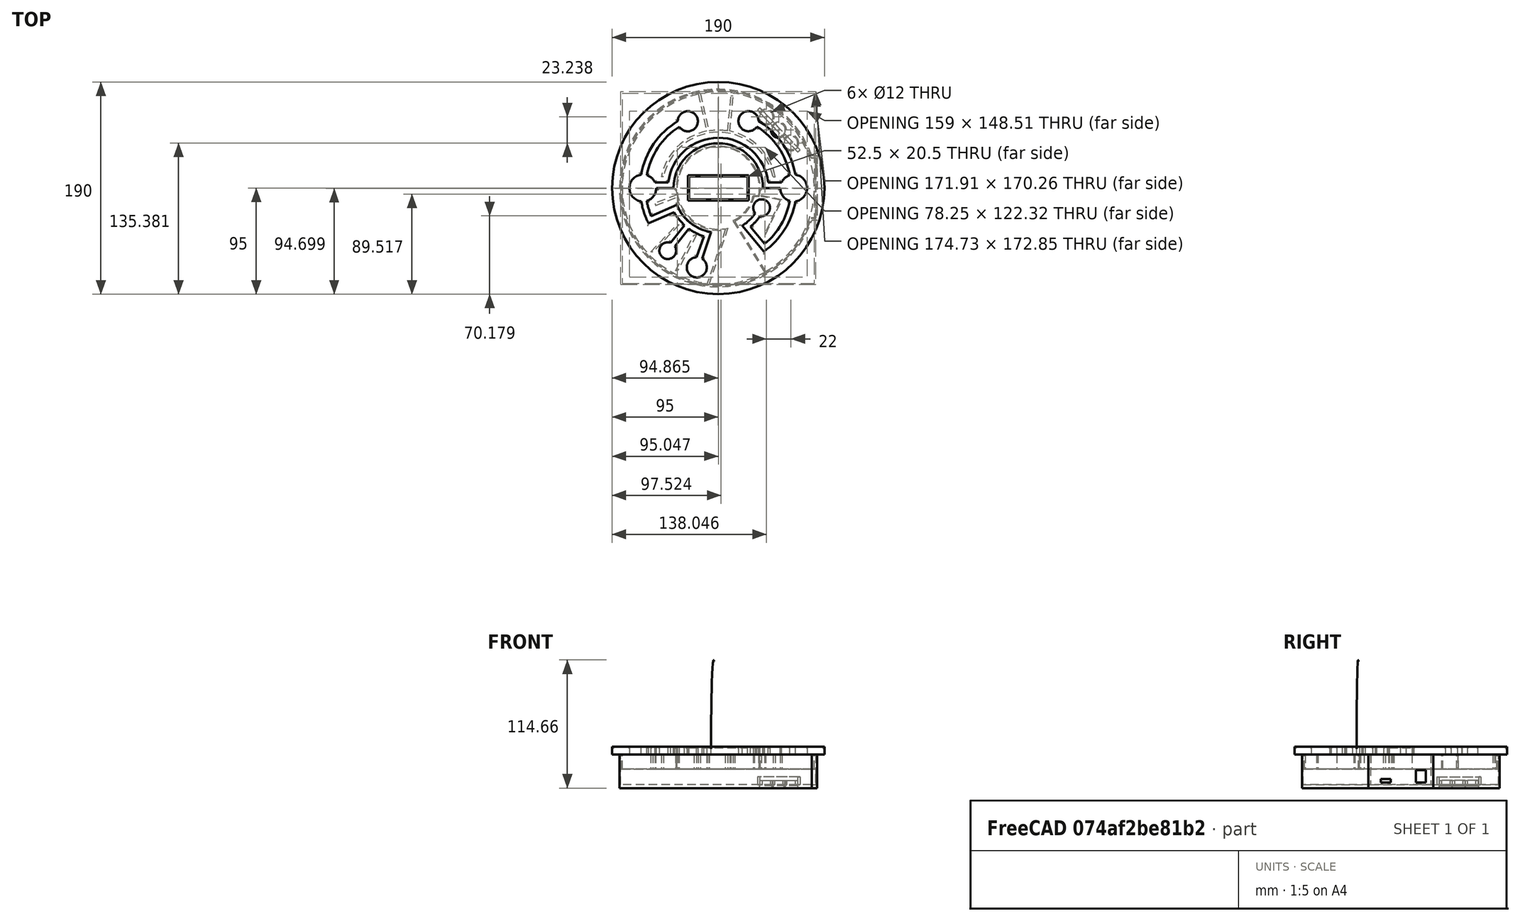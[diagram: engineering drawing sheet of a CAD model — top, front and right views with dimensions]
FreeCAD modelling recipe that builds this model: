
FCSTD DOCUMENT  (FreeCAD 0.18.4R)
Label: 3d-plate-model
License: All rights reserved
LicenseURL: http://en.wikipedia.org/wiki/All_rights_reserved
objects: Sketcher::SketchObject×11, PartDesign::Pad×7, PartDesign::Body×7, PartDesign::Pocket×4, Part::Chamfer×2, Part::Fillet×1
note: 43 computed .brp shape members not serialized (recipe doc carries the construction recipe); baked Part::Feature solids carry a one-line shape summary decoded from their .brp

FEATURE [Sketcher::SketchObject] Sketch  label="master"
  MapMode = 5
  Support = -> [XY_Plane]
  sketch-geometry (43):
    g0: Circle CenterX=9e-16 CenterY=0 CenterZ=0 NormalX=0 NormalY=0 NormalZ=1 AngleXU=0 Radius=95
    g1: LineSegment StartX=-26.25 StartY=10.25 StartZ=0 EndX=26.25 EndY=10.25 EndZ=0
    g2: LineSegment StartX=26.25 StartY=10.25 StartZ=0 EndX=26.25 EndY=-10.25 EndZ=0
    g3: LineSegment StartX=26.25 StartY=-10.25 StartZ=0 EndX=-26.25 EndY=-10.25 EndZ=0
    g4: LineSegment StartX=-26.25 StartY=-10.25 StartZ=0 EndX=-26.25 EndY=10.25 EndZ=0
    g5: ArcOfCircle CenterX=9e-16 CenterY=0 CenterZ=0 NormalX=0 NormalY=0 NormalZ=1 AngleXU=0 Radius=40 StartAngle=0 EndAngle=3.14159
    g6: LineSegment StartX=40 StartY=0 StartZ=0 EndX=55.5 EndY=1.5e-15 EndZ=0
    g7: ArcOfCircle CenterX=9e-16 CenterY=0 CenterZ=0 NormalX=0 NormalY=0 NormalZ=1 AngleXU=0 Radius=45 StartAngle=0.111341 EndAngle=3.0327
    g8: LineSegment StartX=-40 StartY=4.9e-15 StartZ=0 EndX=-55.5 EndY=-3.49e-14 EndZ=0
    g9: LineSegment StartX=-56.5417 StartY=4.89029 StartZ=0 EndX=-44.7335 EndY=4.89029 EndZ=0
    g10: LineSegment StartX=44.7214 StartY=5 StartZ=0 EndX=56.5913 EndY=5 EndZ=0
    g11: ArcOfCircle CenterX=9e-16 CenterY=0 CenterZ=0 NormalX=0 NormalY=0 NormalZ=1 AngleXU=0 Radius=65 StartAngle=0.177422 EndAngle=1.00873
    g12: ArcOfCircle CenterX=9e-16 CenterY=0 CenterZ=0 NormalX=0 NormalY=0 NormalZ=1 AngleXU=0 Radius=65 StartAngle=5.40555 EndAngle=6.10576
    g13: ArcOfCircle CenterX=27.0568 CenterY=59.8456 CenterZ=0 NormalX=0 NormalY=0 NormalZ=1 AngleXU=0 Radius=9 StartAngle=0.017152 EndAngle=5.71464
    g14: ArcOfCircle CenterX=9e-16 CenterY=0 CenterZ=0 NormalX=0 NormalY=0 NormalZ=1 AngleXU=0 Radius=70 StartAngle=5.33406 EndAngle=6.11223
    g15: LineSegment StartX=21.5122 StartY=-33.7228 StartZ=0 EndX=40.7676 EndY=-56.9035 EndZ=0
    g16: ArcOfCircle CenterX=9e-16 CenterY=0 CenterZ=0 NormalX=0 NormalY=0 NormalZ=1 AngleXU=0 Radius=40 StartAngle=5.28022 EndAngle=5.68578
    g17: ArcOfCircle CenterX=38.7698 CenterY=-17.6231 CenterZ=0 NormalX=0 NormalY=0 NormalZ=1 AngleXU=0 Radius=7.5 StartAngle=4.53097 EndAngle=10.1327
    g18: ArcOfCircle CenterX=9e-16 CenterY=0 CenterZ=0 NormalX=0 NormalY=0 NormalZ=1 AngleXU=0 Radius=45 StartAngle=5.40555 EndAngle=5.69415
    g19: LineSegment StartX=28.7537 StartY=-34.6154 StartZ=0 EndX=41.5331 EndY=-50 EndZ=0
    g20: ArcOfCircle CenterX=9e-16 CenterY=0 CenterZ=0 NormalX=0 NormalY=0 NormalZ=1 AngleXU=0 Radius=65 StartAngle=2.13603 EndAngle=2.96417
    g21: ArcOfCircle CenterX=9e-16 CenterY=0 CenterZ=0 NormalX=0 NormalY=0 NormalZ=1 AngleXU=0 Radius=65 StartAngle=3.31901 EndAngle=3.53638
    g22: ArcOfCircle CenterX=-27.2386 CenterY=59.7487 CenterZ=0 NormalX=0 NormalY=0 NormalZ=1 AngleXU=0 Radius=9 StartAngle=3.71182 EndAngle=9.40904
    g23: ArcOfCircle CenterX=9e-16 CenterY=0 CenterZ=0 NormalX=0 NormalY=0 NormalZ=1 AngleXU=0 Radius=70 StartAngle=3.31254 EndAngle=3.60903
    g24: LineSegment StartX=-37.081 StartY=-15 StartZ=0 EndX=-60 EndY=-25 EndZ=0
    g25: ArcOfCircle CenterX=9e-16 CenterY=0 CenterZ=0 NormalX=0 NormalY=0 NormalZ=1 AngleXU=0 Radius=40 StartAngle=3.52599 EndAngle=4.55135
    g26: LineSegment StartX=-62.4908 StartY=-31.542 StartZ=0 EndX=-39.5209 EndY=-21.5198 EndZ=0
    g27: ArcOfCircle CenterX=9e-16 CenterY=0 CenterZ=0 NormalX=0 NormalY=0 NormalZ=1 AngleXU=0 Radius=45 StartAngle=3.64022 EndAngle=3.97511
    g28: LineSegment StartX=-30.2523 StartY=-33.3136 StartZ=0 EndX=-42.6889 EndY=-48.9941 EndZ=0
    g29: LineSegment StartX=-38.8064 StartY=-52.1447 StartZ=0 EndX=-26.3698 EndY=-36.4641 EndZ=0
    g30: ArcOfCircle CenterX=-45.2032 CenterY=-56.0601 CenterZ=0 NormalX=0 NormalY=0 NormalZ=1 AngleXU=0 Radius=7.5 StartAngle=1.22894 EndAngle=6.83245
    g31: ArcOfCircle CenterX=9e-16 CenterY=0 CenterZ=0 NormalX=0 NormalY=0 NormalZ=1 AngleXU=0 Radius=45 StartAngle=4.08628 EndAngle=4.42118
    g32: LineSegment StartX=-12.9201 StartY=-43.1053 StartZ=0 EndX=-19.3775 EndY=-62.0487 EndZ=0
    g33: LineSegment StartX=-6.4138 StartY=-39.4824 StartZ=0 EndX=-14.55 EndY=-63.3506 EndZ=0
    g34: ArcOfCircle CenterX=-19.215 CenterY=-71.0472 CenterZ=0 NormalX=0 NormalY=0 NormalZ=1 AngleXU=0 Radius=9 StartAngle=1.58885 EndAngle=7.30908
    g35: ArcOfCircle CenterX=-67.5 CenterY=0 CenterZ=0 NormalX=0 NormalY=0 NormalZ=1 AngleXU=0 Radius=12 StartAngle=1.69441 EndAngle=4.58877
    g36: ArcOfCircle CenterX=9e-16 CenterY=0 CenterZ=0 NormalX=0 NormalY=0 NormalZ=1 AngleXU=0 Radius=70 StartAngle=2.11493 EndAngle=2.97064
    g37: ArcOfCircle CenterX=-67.5 CenterY=0 CenterZ=0 NormalX=0 NormalY=0 NormalZ=1 AngleXU=0 Radius=12 StartAngle=0.419741 EndAngle=1.27305
    g38: ArcOfCircle CenterX=-67.5 CenterY=0 CenterZ=0 NormalX=0 NormalY=0 NormalZ=1 AngleXU=0 Radius=12 StartAngle=5.01013 EndAngle=6.28319
    g39: ArcOfCircle CenterX=67.5 CenterY=0 CenterZ=0 NormalX=0 NormalY=0 NormalZ=1 AngleXU=0 Radius=12 StartAngle=4.83601 EndAngle=7.73036
    g40: ArcOfCircle CenterX=9e-16 CenterY=0 CenterZ=0 NormalX=0 NormalY=0 NormalZ=1 AngleXU=0 Radius=70 StartAngle=0.170952 EndAngle=1.0297
    g41: ArcOfCircle CenterX=67.5 CenterY=0 CenterZ=0 NormalX=0 NormalY=0 NormalZ=1 AngleXU=0 Radius=12 StartAngle=1.86854 EndAngle=2.71182
    g42: ArcOfCircle CenterX=67.5 CenterY=0 CenterZ=0 NormalX=0 NormalY=0 NormalZ=1 AngleXU=0 Radius=12 StartAngle=3.14159 EndAngle=4.41465
  constraints (133):
    c: Radius(g0) = 95
    c: Coincident(g1,g2)
    c: Coincident(g2,g3)
    c: Coincident(g3,g4)
    c: Coincident(g4,g1)
    c: Horizontal(g1)
    c: Vertical(g4)
    c: DistanceX(g1,g1) = 52.5
    c: DistanceY(g2,g2) = 20.5
    c: Symmetric(g2,g3,g-2)
    c: Symmetric(g2,g1,g-1)
    c: Radius(g5) = 40
    c: Coincident(g5,g0)
    c: Symmetric(g5,g5,g-2)
    c: Parallel(g6,g-1)
    c: PointOnObject(g5,g-1)
    c: Radius(g7) = 45
    c: Coincident(g7,g0)
    c: Parallel(g9,g8)
    c: Coincident(g7,g9)
    c: Coincident(g8,g5)
    c: Parallel(g8,g3)
    c: Coincident(g5,g6)
    c: Coincident(g10,g7)
    c: Parallel(g10,g3)
    c: DistanceY(g6,g10) = 5
    c: Coincident(g11,g0)
    c: Radius(g11) = 65
    c: Coincident(g0,g-1)
    c: Coincident(g12,g0)
    c: Radius(g12) = 65
    c: Coincident(g13,g11)
    c: Radius(g13) = 9
    c: Coincident(g14,g0)
    c: Coincident(g15,g14)
    c: Coincident(g16,g0)
    c: Coincident(g16,g15)
    c: Coincident(g17,g16)
    c: Coincident(g18,g0)
    c: Coincident(g18,g17)
    c: Radius(g16) = 40
    c: Radius(g18) = 45
    c: Coincident(g19,g12)
    c: Coincident(g19,g18)
    c: Parallel(g19,g15)
    c: Radius(g17) = 7.5
    c: Radius(g14) = 70
    c: Distance(g18,g15) = 5
    c: DistanceY(g12,g6) = 50
    c: Perpendicular(g12,g19)
    c: DistanceY(g10,g11) = 50
    c: DistanceY(g7,g13) = 55
    c: DistanceY(g17,g5) = 25
    c: DistanceY(g16,g5) = 22.5
    c: Coincident(g20,g0)
    c: Radius(g20) = 65
    c: Coincident(g21,g0)
    c: Radius(g21) = 65
    c: Coincident(g22,g20)
    c: Radius(g22) = 9
    c: Coincident(g23,g0)
    c: Radius(g23) = 70
    c: DistanceY(g7,g20) = 50
    c: DistanceY(g7,g22) = 55
    c: DistanceY(g21,g5) = 25
    c: Coincident(g24,g21)
    c: Coincident(g25,g0)
    c: Coincident(g25,g24)
    c: Radius(g25) = 40
    c: Coincident(g26,g23)
    c: Coincident(g27,g0)
    c: Radius(g27) = 45
    c: Coincident(g26,g27)
    c: Parallel(g24,g26)
    c: Distance(g26,g24) = 5
    c: DistanceY(g24,g5) = 15
    c: Coincident(g28,g27)
    c: Coincident(g28,g30)
    c: Coincident(g29,g30)
    c: Parallel(g28,g29)
    c: Distance(g29,g27) = 5
    c: Radius(g30) = 7.5
    c: Equal(g28,g29)
    c: Coincident(g31,g0)
    c: Coincident(g31,g29)
    c: Coincident(g32,g31)
    c: Coincident(g33,g25)
    c: Radius(g31) = 45
    c: Coincident(g34,g32)
    c: Parallel(g32,g33)
    c: Coincident(g34,g33)
    c: Equal(g29,g32)
    c: Radius(g34) = 9
    c: Distance(g29,g0) = 65
    c: Distance(g27,g26) = 15
    c: Distance(g23,g30) = 30
    c: Distance(g29,g31) = 15
    c: Distance(g34,g30) = 30
    c: Distance(g33,g32) = 5
    c: Distance(g33,g0) = 65
    c: Coincident(g35,g23)
    c: Distance(g35,g0) = 67.5
    c: Coincident(g36,g0)
    c: Radius(g36) = 70
    c: Coincident(g36,g22)
    c: Coincident(g36,g35)
    c: Radius(g35) = 12
    c: Coincident(g37,g35)
    c: Radius(g37) = 12
    c: Coincident(g37,g20)
    c: Coincident(g37,g9)
    c: Radius(g38) = 12
    c: Coincident(g38,g8)
    c: Coincident(g38,g21)
    c: Coincident(g38,g35)
    c: Distance(g9,g8) = 5
    c: PointOnObject(g35,g-1)
    c: Coincident(g39,g14)
    c: Distance(g39,g0) = 67.5
    c: Coincident(g40,g39)
    c: Coincident(g40,g13)
    c: Coincident(g40,g0)
    c: Radius(g40) = 70
    c: Radius(g39) = 12
    c: PointOnObject(g39,g-1)
    c: Coincident(g41,g39)
    c: Radius(g41) = 12
    c: Coincident(g11,g41)
    c: Coincident(g41,g10)
    c: Coincident(g42,g6)
    c: Coincident(g42,g12)
    c: Coincident(g42,g39)
    c: Radius(g42) = 12
FEATURE [PartDesign::Pad] Pad
  Length = 7
  Length2 = 100
  Profile = -> Sketch
  Type = 0
FEATURE [PartDesign::Body] Body
  Group = -> [Sketch,Pad]
  Origin = -> Origin
  Tip = -> Pad
FEATURE [Sketcher::SketchObject] Sketch003
  sketch-geometry (32):
    g0: ArcOfCircle CenterX=0 CenterY=0 CenterZ=0 NormalX=0 NormalY=0 NormalZ=1 AngleXU=0 Radius=50 StartAngle=0.201358 EndAngle=2.94023
    g1: LineSegment StartX=-48.9898 StartY=10 StartZ=0 EndX=-50.9898 EndY=10 EndZ=0
    g2: LineSegment StartX=48.9898 StartY=10 StartZ=0 EndX=50.9898 EndY=10 EndZ=0
    g3: ArcOfCircle CenterX=0 CenterY=0 CenterZ=0 NormalX=0 NormalY=0 NormalZ=1 AngleXU=0 Radius=51.9611 StartAngle=1.77252 EndAngle=2.94793
    g4: LineSegment StartX=-17.768 StartY=84.1445 StartZ=0 EndX=-10.4109 EndY=50.9075 EndZ=0
    g5: LineSegment StartX=-15.9186 StartY=84.5139 StartZ=0 EndX=-8.51361 EndY=51.0603 EndZ=0
    g6: ArcOfCircle CenterX=0 CenterY=0 CenterZ=0 NormalX=0 NormalY=0 NormalZ=1 AngleXU=0 Radius=51.7652 StartAngle=1.40611 EndAngle=1.73601
    g7: LineSegment StartX=8.48639 StartY=51.0648 StartZ=0 EndX=11.3465 EndY=82.4916 EndZ=0
    g8: ArcOfCircle CenterX=0 CenterY=0 CenterZ=0 NormalX=0 NormalY=0 NormalZ=1 AngleXU=0 Radius=51.9611 StartAngle=0.19366 EndAngle=1.36773
    g9: LineSegment StartX=10.479 StartY=50.8935 StartZ=0 EndX=13.3382 EndY=82.3103 EndZ=0
    g10: ArcOfCircle CenterX=0 CenterY=0 CenterZ=0 NormalX=0 NormalY=0 NormalZ=1 AngleXU=0 Radius=86 StartAngle=5.22955 EndAngle=8.04016
    g11: LineSegment StartX=13.3382 StartY=82.3103 StartZ=0 EndX=11.3465 EndY=82.4916 EndZ=0
    g12: LineSegment StartX=41.647 StartY=-75.2431 StartZ=0 EndX=13.274 EndY=-29.117 EndZ=0
    g13: ArcOfCircle CenterX=0 CenterY=0 CenterZ=0 NormalX=0 NormalY=0 NormalZ=1 AngleXU=0 Radius=32 StartAngle=5.14012 EndAngle=6.06899
    g14: LineSegment StartX=42.5198 StartY=-74.7534 StartZ=0 EndX=14.7086 EndY=-29.5408 EndZ=0
    g15: ArcOfCircle CenterX=0 CenterY=0 CenterZ=0 NormalX=0 NormalY=0 NormalZ=1 AngleXU=0 Radius=33 StartAngle=5.17436 EndAngle=6.05441
    g16: LineSegment StartX=32.1402 StartY=-7.48396 StartZ=0 EndX=36.8177 EndY=-7.48396 EndZ=0
    g17: LineSegment StartX=31.2688 StartY=-6.80182 StartZ=0 EndX=36.2283 EndY=-6.80182 EndZ=0
    g18: ArcOfCircle CenterX=0 CenterY=0 CenterZ=0 NormalX=0 NormalY=0 NormalZ=1 AngleXU=0 Radius=36.8613 StartAngle=6.0976 EndAngle=11.23
    g19: ArcOfCircle CenterX=0 CenterY=0 CenterZ=0 NormalX=0 NormalY=0 NormalZ=1 AngleXU=0 Radius=37.8156 StartAngle=3.3603 EndAngle=4.88018
    g20: LineSegment StartX=6.31521 StartY=-37.2846 StartZ=0 EndX=-9.8724 EndY=-85.4315 EndZ=0
    g21: LineSegment StartX=8.56275 StartY=-35.853 StartZ=0 EndX=-8.16667 EndY=-85.6114 EndZ=0
    g22: ArcOfCircle CenterX=0 CenterY=0 CenterZ=0 NormalX=0 NormalY=0 NormalZ=1 AngleXU=0 Radius=86 StartAngle=1.7789 EndAngle=4.59734
    g23: LineSegment StartX=-37.0686 StartY=-6.12106 StartZ=0 EndX=-56.6237 EndY=-13.6379 EndZ=0
    g24: LineSegment StartX=-56.6237 StartY=-13.6379 StartZ=0 EndX=-55.9061 EndY=-15.5047 EndZ=0
    g25: LineSegment StartX=-55.9061 StartY=-15.5047 StartZ=0 EndX=-36.9149 EndY=-8.20461 EndZ=0
    g26: ArcOfCircle CenterX=0 CenterY=0 CenterZ=0 NormalX=0 NormalY=0 NormalZ=1 AngleXU=0 Radius=37.5706 StartAngle=6.08265 EndAngle=9.58843
    g27: ArcOfCircle CenterX=0 CenterY=0 CenterZ=0 NormalX=0 NormalY=0 NormalZ=1 AngleXU=0 Radius=86 StartAngle=4.61728 EndAngle=5.21791
    g28: ArcOfCircle CenterX=0 CenterY=0 CenterZ=0 NormalX=0 NormalY=0 NormalZ=1 AngleXU=0 Radius=87.22 StartAngle=0.312342 EndAngle=5.97209
    g29: LineSegment StartX=83 StartY=26.8016 StartZ=0 EndX=87.1 EndY=26.8016 EndZ=0
    g30: LineSegment StartX=87.1 StartY=26.8016 StartZ=0 EndX=87.1 EndY=-26.6984 EndZ=0
    g31: LineSegment StartX=87.1 StartY=-26.6984 StartZ=0 EndX=83.0333 EndY=-26.6984 EndZ=0
  constraints (96):
    c: Coincident(g0,g-1)
    c: Coincident(g1,g0)
    c: Horizontal(g2)
    c: Coincident(g0,g2)
    c: Coincident(g3,g0)
    c: Coincident(g3,g1)
    c: Parallel(g1,g-1)
    c: Distance(g1) = 2
    c: Distance(g0,g0) = 50
    c: DistanceY(g-1,g0) = 10
    c: Coincident(g4,g3)
    c: Coincident(g6,g0)
    c: Coincident(g5,g6)
    c: Parallel(g5,g4)
    c: DistanceY(g-1,g0) = 10
    c: Distance(g2) = 2
    c: Coincident(g6,g7)
    c: Coincident(g8,g0)
    c: Coincident(g8,g2)
    c: Coincident(g9,g8)
    c: Distance(g8,g6) = 2
    c: Parallel(g7,g9)
    c: Distance(g5,g6) = 17
    c: Distance(g3,g8) = 20.89
    c: Coincident(g10,g0)
    c: Distance(g3,g1) = 57.62
    c: Distance(g10,g0) = 85
    c: Coincident(g11,g7)
    c: Coincident(g9,g11)
    c: Perpendicular(g9,g11)
    c: Coincident(g13,g0)
    c: Coincident(g13,g12)
    c: Coincident(g14,g10)
    c: Coincident(g15,g0)
    c: Coincident(g15,g14)
    c: Parallel(g14,g12)
    c: Distance(g10,g12) = 1
    c: Distance(g13,g0) = 32
    c: Distance(g15,g0) = 33
    c: Coincident(g16,g15)
    c: Horizontal(g17)
    c: Coincident(g17,g13)
    c: Parallel(g17,g16)
    c: Coincident(g18,g0)
    c: Coincident(g18,g17)
    c: Coincident(g19,g0)
    c: Distance(g13,g0) = 24.42
    c: Coincident(g20,g19)
    c: Coincident(g21,g18)
    c: Parallel(g21,g20)
    c: Coincident(g22,g0)
    c: Coincident(g22,g20)
    c: Coincident(g22,g4)
    c: Distance(g18,g12) = 8.22
    c: Distance(g18,g14) = 8.81
    c: Distance(g19,g12) = 10.73
    c: Distance(g19,g14) = 11.42
    c: Coincident(g24,g23)
    c: Perpendicular(g23,g24)
    c: Distance(g24) = 2
    c: Coincident(g25,g24)
    c: Parallel(g23,g25)
    c: Distance(g23) = 20.95
    c: Distance(g23,g0) = 24.84
    c: Distance(g1,g23) = 24.3
    c: Coincident(g26,g16)
    c: Coincident(g26,g0)
    c: Coincident(g19,g25)
    c: Coincident(g26,g23)
    c: Distance(g14,g16) = 31.23
    c: Distance(g13,g14) = 28.13
    c: Distance(g23,g0) = 20.05
    c: Coincident(g10,g5)
    c: Coincident(g27,g0)
    c: Coincident(g27,g21)
    c: Coincident(g27,g12)
    c: Radius(g27) = 86
    c: Radius(g22) = 86
    c: Radius(g10) = 86
    c: Distance(g7,g5) = 37.18
    c: Distance(g7,g8) = 31.61
    c: Distance(g9,g6) = 31.62
    c: Coincident(g28,g0)
    c: Radius(g28) = 87.22
    c: Horizontal(g29)
    c: Coincident(g29,g30)
    c: Coincident(g30,g31)
    c: Parallel(g31,g29)
    c: Perpendicular(g-1,g30)
    c: Coincident(g31,g28)
    c: Coincident(g29,g28)
    c: Distance(g0,g30) = 87.1
    c: Distance(g30) = 53.5
    c: Distance(g5,g7) = 27.34
    c: Distance(g21,g19) = 50.45
    c: Distance(g29) = 4.1
FEATURE [PartDesign::Pad] Pad002
  Length = 13
  Length2 = 100
  Profile = -> Sketch003
  Reversed = true
  Type = 0
FEATURE [PartDesign::Body] Body002
  Group = -> [Sketch003,Pad002]
  Origin = -> Origin002
  Tip = -> Pad002
FEATURE [Sketcher::SketchObject] Sketch004
  MapMode = 5
  Support = -> [XY_Plane003]
  sketch-geometry (6):
    g0: LineSegment StartX=38.4582 StartY=-6.538 StartZ=0 EndX=56.9397 EndY=-10.1656 EndZ=0
    g1: LineSegment StartX=55.503 StartY=-10.8836 StartZ=0 EndX=41.5429 EndY=-40.9033 EndZ=0
    g2: LineSegment StartX=42.4533 StartY=-41.317 StartZ=0 EndX=56.9397 EndY=-10.1656 EndZ=0
    g3: LineSegment StartX=41.5429 StartY=-40.9033 StartZ=0 EndX=42.4533 EndY=-41.317 EndZ=0
    g4: LineSegment StartX=55.503 StartY=-10.8836 StartZ=0 EndX=38.4582 EndY=-7.538 EndZ=0
    g5: LineSegment StartX=38.4582 StartY=-7.538 StartZ=0 EndX=38.4582 EndY=-6.538 EndZ=0
  constraints (18):
    c: Coincident(g5,g0)
    c: Coincident(g5,g4)
    c: Coincident(g4,g1)
    c: Coincident(g3,g1)
    c: Coincident(g3,g2)
    c: Coincident(g0,g2)
    c: Distance(g5) = 1
    c: Distance(g3) = 1
    c: Parallel(g0,g4)
    c: Parallel(g2,g1)
    c: Distance(g1,g0) = 17.59
    c: Perpendicular(g-1,g5)
    c: Distance(g-1,g0) = 39.01
    c: Distance(g-1,g4) = 39.19
    c: Distance(g-1,g0) = 57.84
    c: Distance(g-1,g1) = 56.56
    c: Distance(g-1,g1) = 58.3
    c: Distance(g-1,g2) = 59.24
FEATURE [PartDesign::Pad] Pad003
  Length = 13
  Length2 = 100
  Profile = -> Sketch004
  Reversed = true
  Type = 0
FEATURE [PartDesign::Body] Body003
  Group = -> [Sketch004,Pad003]
  Origin = -> Origin003
  Tip = -> Pad003
FEATURE [Sketcher::SketchObject] Sketch005
  MapMode = 5
  Support = -> [XY_Plane004]
  sketch-geometry (4):
    g0: LineSegment StartX=-38.251 StartY=-73.9195 StartZ=0 EndX=-21.592 EndY=-42.0167 EndZ=0
    g1: LineSegment StartX=-21.592 StartY=-42.0167 StartZ=0 EndX=-19.592 EndY=-42.0167 EndZ=0
    g2: LineSegment StartX=-19.592 StartY=-42.0167 StartZ=0 EndX=-36.251 EndY=-73.9195 EndZ=0
    g3: LineSegment StartX=-36.251 StartY=-73.9195 StartZ=0 EndX=-38.251 EndY=-73.9195 EndZ=0
  constraints (12):
    c: Coincident(g0,g1)
    c: Coincident(g1,g2)
    c: Coincident(g2,g3)
    c: Coincident(g3,g0)
    c: Parallel(g0,g2)
    c: Parallel(g1,g3)
    c: Parallel(g1,g-1)
    c: Distance(g3) = 2
    c: Distance(g-1,g1) = 46.36
    c: Distance(g-1,g0) = 47.24
    c: Distance(g-1,g2) = 82.33
    c: Distance(g-1,g0) = 83.23
FEATURE [PartDesign::Pad] Pad004
  Length = 13
  Length2 = 100
  Profile = -> Sketch005
  Reversed = true
  Type = 0
FEATURE [PartDesign::Body] Body004
  Group = -> [Sketch005,Pad004]
  Origin = -> Origin004
  Tip = -> Pad004
FEATURE [Sketcher::SketchObject] Sketch006
  MapMode = 5
  Support = -> [XY_Plane005]
  sketch-geometry (4):
    g0: LineSegment StartX=-36.9862 StartY=-32.702 StartZ=0 EndX=-34.9862 EndY=-32.702 EndZ=0
    g1: LineSegment StartX=-34.9862 StartY=-32.702 StartZ=0 EndX=-58.5224 EndY=-57.3666 EndZ=0
    g2: LineSegment StartX=-58.5224 StartY=-57.3666 StartZ=0 EndX=-60.5224 EndY=-57.3666 EndZ=0
    g3: LineSegment StartX=-60.5224 StartY=-57.3666 StartZ=0 EndX=-36.9862 EndY=-32.702 EndZ=0
  constraints (12):
    c: Coincident(g0,g1)
    c: Coincident(g1,g2)
    c: Coincident(g2,g3)
    c: Coincident(g3,g0)
    c: Parallel(g0,g2)
    c: Parallel(g3,g1)
    c: Distance(g0) = 2
    c: Parallel(g0,g-1)
    c: Distance(g-1,g0) = 47.89
    c: Distance(g-1,g0) = 49.37
    c: Distance(g-1,g1) = 81.95
    c: Distance(g-1,g2) = 83.39
FEATURE [PartDesign::Pad] Pad005
  Length = 13
  Length2 = 100
  Profile = -> Sketch006
  Reversed = true
  Type = 0
FEATURE [PartDesign::Body] Body005
  Group = -> [Sketch006,Pad005]
  Origin = -> Origin005
  Tip = -> Pad005
FEATURE [Sketcher::SketchObject] Sketch007
  MapMode = 5
  Support = -> [XY_Plane006]
  sketch-geometry (7):
    g0: Circle CenterX=43.0463 CenterY=63.619 CenterZ=0 NormalX=0 NormalY=0 NormalZ=1 AngleXU=0 Radius=6
    g1: Circle CenterX=54.0463 CenterY=52 CenterZ=0 NormalX=0 NormalY=0 NormalZ=1 AngleXU=0 Radius=6
    g2: Circle CenterX=65.0463 CenterY=40.381 CenterZ=0 NormalX=0 NormalY=0 NormalZ=1 AngleXU=0 Radius=6
    g3: ArcOfCircle CenterX=0 CenterY=0 CenterZ=0 NormalX=0 NormalY=0 NormalZ=1 AngleXU=0 Radius=88.5 StartAngle=0.333851 EndAngle=5.94933
    g4: LineSegment StartX=83.6137 StartY=29 StartZ=0 EndX=88.6137 EndY=29 EndZ=0
    g5: LineSegment StartX=88.6137 StartY=29 StartZ=0 EndX=88.6137 EndY=-29 EndZ=0
    g6: LineSegment StartX=88.6137 StartY=-29 StartZ=0 EndX=83.6137 EndY=-29 EndZ=0
  constraints (21):
    c: Radius(g0) = 6
    c: Radius(g1) = 6
    c: Radius(g2) = 6
    c: Distance(g2,g1) = 16
    c: Coincident(g3,g-1)
    c: Radius(g3) = 88.5
    c: Horizontal(g4)
    c: Vertical(g5)
    c: Coincident(g4,g3)
    c: Coincident(g5,g4)
    c: Coincident(g6,g5)
    c: Parallel(g6,g-1)
    c: Coincident(g3,g6)
    c: Distance(g5) = 58
    c: DistanceY(g-1,g3) = 29
    c: Distance(g4) = 5
    c: Distance(g1,g3) = 75
    c: DistanceX(g0,g1) = 11
    c: Distance(g1,g0) = 16
    c: DistanceX(g1,g2) = 11
    c: DistanceY(g3,g1) = 52
FEATURE [PartDesign::Pad] Pad006
  Length = 30
  Length2 = 100
  Profile = -> Sketch007
  Reversed = true
  Type = 0
FEATURE [Sketcher::SketchObject] Sketch008
  MapMode = 5
  Support = -> [XY_Plane006]
  sketch-geometry (4):
    g0: ArcOfCircle CenterX=0 CenterY=0 CenterZ=0 NormalX=0 NormalY=0 NormalZ=1 AngleXU=0 Radius=87.5 StartAngle=0.313691 EndAngle=5.96949
    g1: LineSegment StartX=83.2301 StartY=-27 StartZ=0 EndX=87.2301 EndY=-27 EndZ=0
    g2: LineSegment StartX=87.2301 StartY=-27 StartZ=0 EndX=87.2301 EndY=27 EndZ=0
    g3: LineSegment StartX=87.2301 StartY=27 StartZ=0 EndX=83.2301 EndY=27 EndZ=0
  constraints (12):
    c: Radius(g0) = 87.5
    c: Coincident(g-1,g0)
    c: Coincident(g1,g2)
    c: Vertical(g2)
    c: Coincident(g2,g3)
    c: Parallel(g3,g-1)
    c: Parallel(g-1,g1)
    c: Coincident(g1,g0)
    c: Coincident(g0,g3)
    c: Distance(g1) = 4
    c: Distance(g3) = 4
    c: Distance(g2) = 54
FEATURE [PartDesign::Pocket] Pocket
  BaseFeature = -> Pad006
  Length = 27
  Length2 = 100
  Profile = -> Sketch008
  Type = 0
FEATURE [Sketcher::SketchObject] Sketch009
  MapMode = 5
  Placement = pos=(88.6137,0,0) rot=(0.57735,0.57735,0.57735;2.0944rad)
  Support = -> [Pocket]
  sketch-geometry (8):
    g0: LineSegment StartX=13.5 StartY=-14 StartZ=0 EndX=22.5 EndY=-14 EndZ=0
    g1: LineSegment StartX=22.5 StartY=-14 StartZ=0 EndX=22.5 EndY=-25 EndZ=0
    g2: LineSegment StartX=22.5 StartY=-25 StartZ=0 EndX=13.5 EndY=-25 EndZ=0
    g3: LineSegment StartX=13.5 StartY=-25 StartZ=0 EndX=13.5 EndY=-14 EndZ=0
    g4: LineSegment StartX=-9 StartY=-22 StartZ=0 EndX=-18 EndY=-22 EndZ=0
    g5: LineSegment StartX=-18 StartY=-22 StartZ=0 EndX=-18 EndY=-25 EndZ=0
    g6: LineSegment StartX=-18 StartY=-25 StartZ=0 EndX=-9 EndY=-25 EndZ=0
    g7: LineSegment StartX=-9 StartY=-25 StartZ=0 EndX=-9 EndY=-22 EndZ=0
  constraints (24):
    c: Coincident(g0,g1)
    c: Coincident(g1,g2)
    c: Coincident(g2,g3)
    c: Coincident(g3,g0)
    c: Horizontal(g0)
    c: Horizontal(g2)
    c: Vertical(g1)
    c: Vertical(g3)
    c: Distance(g1) = 11
    c: Distance(g0) = 9
    c: DistanceY(g2,g-1) = 25
    c: DistanceX(g-1,g0) = 13.5
    c: Coincident(g4,g5)
    c: Coincident(g5,g6)
    c: Coincident(g6,g7)
    c: Coincident(g7,g4)
    c: Horizontal(g4)
    c: Horizontal(g6)
    c: Vertical(g5)
    c: Vertical(g7)
    c: DistanceY(g5,g-1) = 25
    c: Distance(g5) = 3
    c: Distance(g4) = 9
    c: DistanceX(g6,g-1) = 9
FEATURE [PartDesign::Pocket] Pocket001
  BaseFeature = -> Pocket
  Length = 2
  Length2 = 100
  Profile = -> Sketch009
  Type = 0
FEATURE [PartDesign::Body] Body006  label="backcover"
  Group = -> [Sketch007,Pad006,Sketch008,Pocket,Sketch009,Pocket001]
  Origin = -> Origin006
  Tip = -> Pocket001
FEATURE [Sketcher::SketchObject] Sketch010
  MapMode = 5
  Support = -> [XY_Plane007]
  sketch-geometry (4):
    g0: LineSegment StartX=35 StartY=69.6857 StartZ=0 EndX=37.1648 EndY=71.7626 EndZ=0
    g1: LineSegment StartX=37.1648 StartY=71.7626 StartZ=0 EndX=73.1648 EndY=34.2393 EndZ=0
    g2: LineSegment StartX=73.1648 StartY=34.2393 StartZ=0 EndX=71 EndY=32.1623 EndZ=0
    g3: LineSegment StartX=71 StartY=32.1623 StartZ=0 EndX=35 EndY=69.6857 EndZ=0
  constraints (12):
    c: Coincident(g0,g1)
    c: Coincident(g1,g2)
    c: Coincident(g2,g3)
    c: Coincident(g3,g0)
    c: Parallel(g3,g1)
    c: Parallel(g0,g2)
    c: Perpendicular(g3,g0)
    c: Distance(g0) = 3
    c: Distance(g-1,g3) = 73.5
    c: Distance(g3) = 52
    c: DistanceX(g-1,g0) = 35
    c: DistanceX(g-1,g2) = 71
FEATURE [PartDesign::Pad] Pad007
  Length = 6
  Length2 = 100
  Profile = -> Sketch010
  Reversed = true
  Type = 3
  UpToFace = -> Pocket001 [Face22]
FEATURE [Sketcher::SketchObject] Sketch011
  MapMode = 5
  Placement = pos=(53.0378,50.8846,0) rot=(0.856349,-0.365148,-0.365148;1.72526rad)
  Support = -> [Pad007]
  sketch-geometry (4):
    g0: LineSegment StartX=-27 StartY=0 StartZ=0 EndX=27 EndY=0 EndZ=0
    g1: LineSegment StartX=27 StartY=0 StartZ=0 EndX=27 EndY=-20 EndZ=0
    g2: LineSegment StartX=27 StartY=-20 StartZ=0 EndX=-27 EndY=-20 EndZ=0
    g3: LineSegment StartX=-27 StartY=-20 StartZ=0 EndX=-27 EndY=0 EndZ=0
  constraints (12):
    c: Coincident(g0,g1)
    c: Coincident(g1,g2)
    c: Coincident(g2,g3)
    c: Coincident(g3,g0)
    c: Horizontal(g0)
    c: Horizontal(g2)
    c: Vertical(g1)
    c: Vertical(g3)
    c: PointOnObject(g-1,g0)
    c: Distance(g0) = 54
    c: Distance(g-1,g0) = 27
    c: Distance(g1) = 20
FEATURE [PartDesign::Pocket] Pocket002
  BaseFeature = -> Pad007
  Length = 3
  Length2 = 100
  Profile = -> Sketch011
  Type = 0
FEATURE [Sketcher::SketchObject] Sketch012
  MapMode = 5
  Placement = pos=(53.0378,50.8846,0) rot=(0.856349,-0.365148,-0.365148;1.72526rad)
  Support = -> [Pocket002]
  sketch-geometry (12):
    g0: LineSegment StartX=-22.75 StartY=-23 StartZ=0 EndX=-9.25 EndY=-23 EndZ=0
    g1: LineSegment StartX=-9.25 StartY=-23 StartZ=0 EndX=-9.25 EndY=-27 EndZ=0
    g2: LineSegment StartX=-9.25 StartY=-27 StartZ=0 EndX=-22.75 EndY=-27 EndZ=0
    g3: LineSegment StartX=-22.75 StartY=-27 StartZ=0 EndX=-22.75 EndY=-23 EndZ=0
    g4: LineSegment StartX=-6.75 StartY=-23 StartZ=0 EndX=6.75 EndY=-23 EndZ=0
    g5: LineSegment StartX=6.75 StartY=-23 StartZ=0 EndX=6.75 EndY=-27 EndZ=0
    g6: LineSegment StartX=6.75 StartY=-27 StartZ=0 EndX=-6.75 EndY=-27 EndZ=0
    g7: LineSegment StartX=-6.75 StartY=-27 StartZ=0 EndX=-6.75 EndY=-23 EndZ=0
    g8: LineSegment StartX=9.25 StartY=-23 StartZ=0 EndX=22.75 EndY=-23 EndZ=0
    g9: LineSegment StartX=22.75 StartY=-23 StartZ=0 EndX=22.75 EndY=-27 EndZ=0
    g10: LineSegment StartX=22.75 StartY=-27 StartZ=0 EndX=9.25 EndY=-27 EndZ=0
    g11: LineSegment StartX=9.25 StartY=-27 StartZ=0 EndX=9.25 EndY=-23 EndZ=0
  constraints (36):
    c: Coincident(g0,g1)
    c: Coincident(g1,g2)
    c: Coincident(g2,g3)
    c: Coincident(g3,g0)
    c: Horizontal(g0)
    c: Horizontal(g2)
    c: Vertical(g1)
    c: Vertical(g3)
    c: Distance(g2) = 13.5
    c: DistanceX(g1,g-1) = 9.25
    c: Distance(g1) = 4
    c: DistanceY(g1,g-1) = 27
    c: Coincident(g4,g5)
    c: Coincident(g5,g6)
    c: Coincident(g6,g7)
    c: Coincident(g7,g4)
    c: Horizontal(g4)
    c: Horizontal(g6)
    c: Vertical(g5)
    c: Vertical(g7)
    c: Distance(g6) = 13.5
    c: DistanceY(g5,g-1) = 27
    c: DistanceY(g7,g7) = 4
    c: DistanceX(g4,g-1) = 6.75
    c: Coincident(g8,g9)
    c: Coincident(g9,g10)
    c: Coincident(g10,g11)
    c: Coincident(g11,g8)
    c: Horizontal(g8)
    c: Horizontal(g10)
    c: Vertical(g9)
    c: Vertical(g11)
    c: Distance(g10) = 13.5
    c: DistanceY(g9,g9) = 4
    c: DistanceY(g10,g-1) = 27
    c: DistanceX(g-1,g10) = 9.25
FEATURE [PartDesign::Pocket] Pocket003
  BaseFeature = -> Pocket002
  Length = 3
  Length2 = 100
  Profile = -> Sketch012
  Type = 0
FEATURE [PartDesign::Body] Body007
  Group = -> [Sketch010,Pad007,Sketch011,Pocket002,Sketch012,Pocket003]
  Origin = -> Origin007
  Tip = -> Pocket003
FEATURE [Part::Fillet] Fillet
  Base = -> Pad
  Edges = 39 edges: [Edge3 r=4,Edge7 r=2,Edge10 r=2,Edge13 r=2,Edge16 r=2,Edge19 r=2,Edge22 r=2,Edge25 r=2,Edge28 r=2,Edge31 r=2,Edge34 r=2,Edge37 r=2,Edge40 r=2,Edge43 r=2,Edge46 r=2,Edge49 r=2,Edge52 r=2,Edge55 r=2,Edge58 r=2,Edge61 r=2,Edge64 r=2,Edge67 r=2,Edge70 r=2,Edge73 r=2,Edge76 r=2,Edge79 r=2,Edge82 r=2,Edge85 r=2,Edge88 r=2,Edge91 r=2,Edge94 r=2,Edge97 r=2,Edge100 r=2,Edge103 r=2,Edge106 r=2,Edge109 r=2,Edge112 r=2,Edge115 r=2,Edge117 r=2]
FEATURE [Part::Chamfer] Chamfer001
  Base = -> Pocket001
  Edges = 3 edges r=1: [Edge44,Edge46,Edge48]
FEATURE [Part::Chamfer] Chamfer
  Base = -> Fillet
  Edges = 4 edges r=1: [Edge48,Edge49,Edge50,Edge51]
